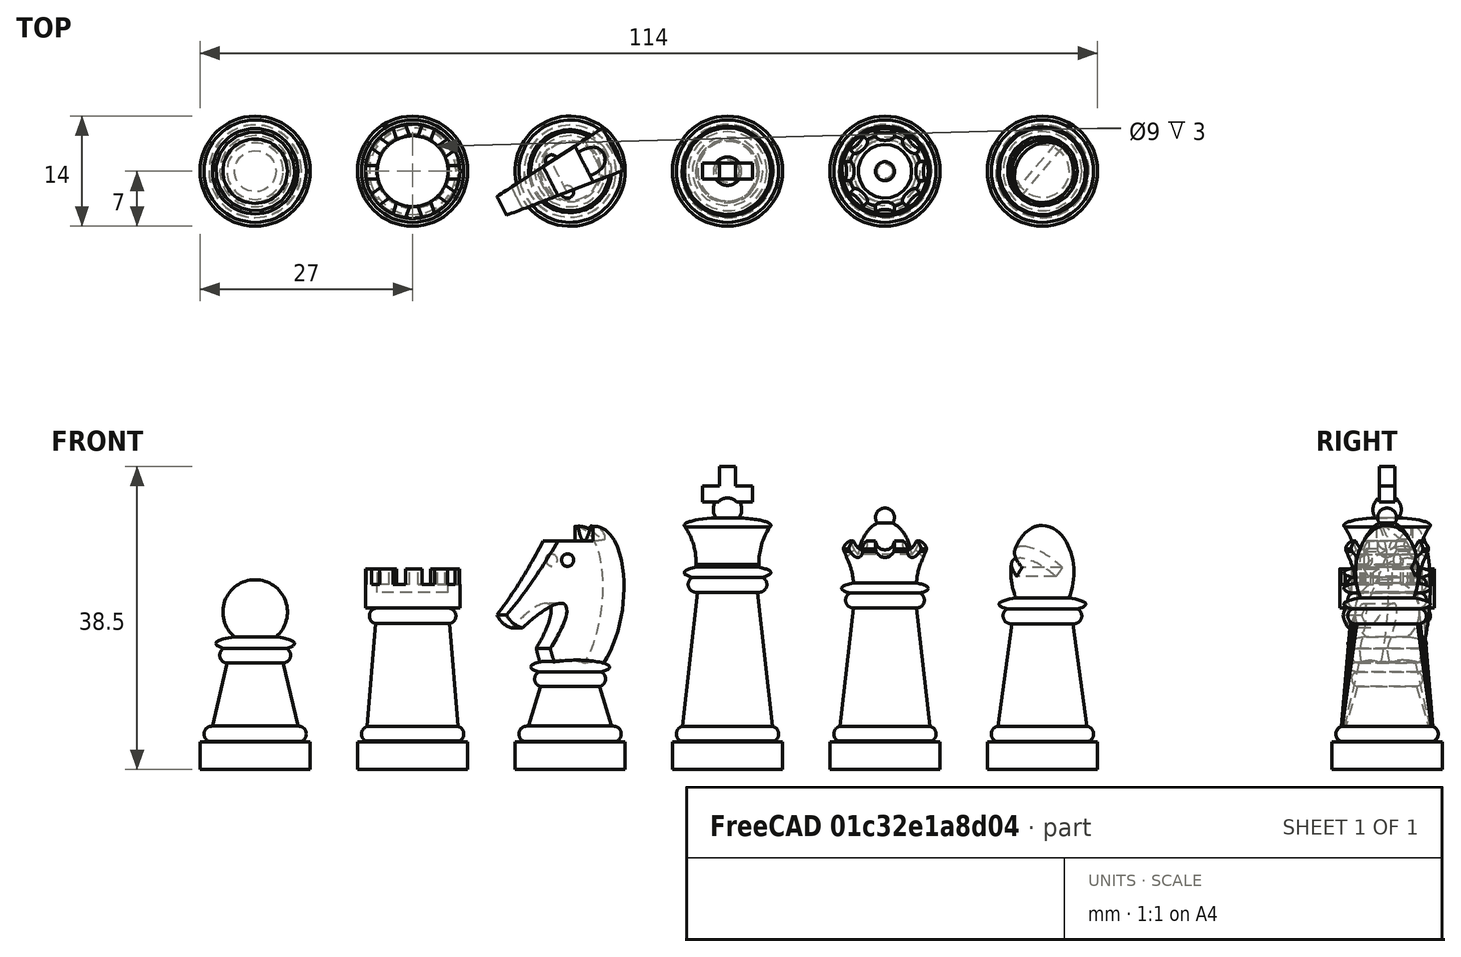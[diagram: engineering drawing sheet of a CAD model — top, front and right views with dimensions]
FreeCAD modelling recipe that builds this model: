
FCSTD DOCUMENT  (FreeCAD 0.15R4671 (Git))
Label: Chess_01
License: All rights reserved
LicenseURL: http://de.wikipedia.org/wiki/Alle_Rechte_vorbehalten
objects: Part::Cut×24, Part::MultiFuse×20, Part::Cylinder×16, Part::Torus×14, Part::Ellipsoid×14, Part::Box×12, Part::Cone×8, Part::Sphere×6, Part::Plane×1, Part::MultiCommon×1
note: 116 computed .brp shape members not serialized (recipe doc carries the construction recipe); baked Part::Feature solids carry a one-line shape summary decoded from their .brp

FEATURE [Part::Cylinder] Cylinder  label="Zylinder"
  Angle = 360
  Height = 3.5
  Radius = 7
FEATURE [Part::Cone] Cone  label="Kegel"
  Angle = 360
  Height = 18
  Placement = pos=(0,0,3) rot=(0,0,1;0rad)
  Radius1 = 6
  Radius2 = 4.5
FEATURE [Part::Cylinder] Cylinder001  label="Zylinder001"
  Angle = 360
  Height = 5
  Placement = pos=(0,0,20.5) rot=(0,0,1;0rad)
  Radius = 6
FEATURE [Part::Torus] Torus
  Angle1 = -180
  Angle2 = 180
  Angle3 = 360
  Placement = pos=(0,0,4.5) rot=(0,0,1;0rad)
  Radius1 = 5.5
  Radius2 = 1
FEATURE [Part::Torus] Torus001
  Angle1 = -180
  Angle2 = 180
  Angle3 = 360
  Placement = pos=(0,0,19.5) rot=(0,0,1;0rad)
  Radius1 = 4.5
  Radius2 = 1
FEATURE [Part::Cylinder] Cylinder002  label="Zylinder002"
  Angle = 360
  Height = 10
  Placement = pos=(0,0,22.5) rot=(0,0,1;0rad)
  Radius = 4.5
FEATURE [Part::Cut] Cut
  Base = -> Cylinder001
  Tool = -> Cylinder002
FEATURE [Part::Box] Box  label="Quader"
  Height = 4
  Length = 14
  Placement = pos=(-7,-1,23.5) rot=(0,0,1;0rad)
  Width = 1.7
FEATURE [Part::Box] Box001  label="Quader001"
  Height = 4
  Length = 14
  Placement = pos=(-5.07533,-4.92351,23.5) rot=(0,0,1;0.628319rad)
  Width = 1.7
FEATURE [Part::Box] Box002  label="Quader002"
  Height = 4
  Length = 14
  Placement = pos=(-1.21206,-6.96641,23.5) rot=(0,0,1;1.25664rad)
  Width = 1.7
FEATURE [Part::Box] Box003  label="Quader003"
  Height = 4
  Length = 14
  Placement = pos=(3.11418,-6.34838,23.5) rot=(0,0,1;1.88496rad)
  Width = 1.7
FEATURE [Part::Box] Box004  label="Quader004"
  Height = 4
  Length = 14
  Placement = pos=(6.2509,-3.30548,23.5) rot=(0,0,1;2.51327rad)
  Width = 1.7
FEATURE [Part::Cut] Cut001
  Base = -> Cut
  Tool = -> Box
FEATURE [Part::Cut] Cut002
  Base = -> Cut001
  Tool = -> Box001
FEATURE [Part::Cut] Cut003
  Base = -> Cut002
  Tool = -> Box002
FEATURE [Part::Cut] Cut004
  Base = -> Cut003
  Tool = -> Box003
FEATURE [Part::Cut] Cut005
  Base = -> Cut004
  Tool = -> Box004
FEATURE [Part::MultiFuse] Fusion
  Shapes = -> [Cone,Cut005]
FEATURE [Part::MultiFuse] Fusion001
  Shapes = -> [Cylinder,Fusion]
FEATURE [Part::MultiFuse] Fusion002
  Shapes = -> [Torus001,Fusion001]
FEATURE [Part::MultiFuse] Fusion003  label="Turm"
  Placement = pos=(40,0,0) rot=(0,0,1;0rad)
  Shapes = -> [Torus,Fusion002]
FEATURE [Part::Cylinder] Cylinder003  label="Zylinder003"
  Angle = 360
  Height = 3.5
  Radius = 7
FEATURE [Part::Cone] Cone001  label="Kegel001"
  Angle = 360
  Height = 18
  Placement = pos=(0,0,3) rot=(0,0,1;0rad)
  Radius1 = 6
  Radius2 = 3.5
FEATURE [Part::Torus] Torus002
  Angle1 = -180
  Angle2 = 180
  Angle3 = 360
  Placement = pos=(0,0,4.5) rot=(0,0,1;0rad)
  Radius1 = 5.5
  Radius2 = 1
FEATURE [Part::Torus] Torus003
  Angle1 = -180
  Angle2 = 180
  Angle3 = 360
  Placement = pos=(0,0,19.5) rot=(0,0,1;0rad)
  Radius1 = 4
  Radius2 = 1
FEATURE [Part::Ellipsoid] Ellipsoid001
  Angle1 = -90
  Angle2 = 90
  Angle3 = 360
  Placement = pos=(0,0,25) rot=(0,0,1;0rad)
  Radius1 = 6
  Radius2 = 4
  Radius3 = 4
FEATURE [Part::Ellipsoid] Ellipsoid
  Angle1 = -90
  Angle2 = 90
  Angle3 = 360
  Placement = pos=(0,0,21) rot=(0,0,1;0rad)
  Radius1 = 1
  Radius2 = 5.5
  Radius3 = 5.5
FEATURE [Part::MultiFuse] Fusion004
  Shapes = -> [Cylinder003,Cone001]
FEATURE [Part::MultiFuse] Fusion005
  Shapes = -> [Fusion004,Torus003]
FEATURE [Part::MultiFuse] Fusion006
  Shapes = -> [Fusion005,Torus002]
FEATURE [Part::MultiFuse] Fusion007
  Shapes = -> [Fusion006,Ellipsoid]
FEATURE [Part::MultiFuse] Fusion008
  Shapes = -> [Fusion007,Ellipsoid001]
FEATURE [Part::Box] Box009  label="Quader005"
  Height = 1.5
  Length = 10
  Placement = pos=(1,-5,24.5) rot=(0,-1,0;0.698132rad)
  Width = 10
FEATURE [Part::Cut] Cut006  label="Laeufer"
  Base = -> Fusion008
  Placement = pos=(120,0,0) rot=(0,0,1;2.44346rad)
  Tool = -> Box009
FEATURE [Part::Plane] Plane  label="Brett"
  Length = 160
  Placement = pos=(-10,-10,0) rot=(0,0,1;0rad)
  Width = 160
FEATURE [Part::Torus] Torus004
  Angle1 = -180
  Angle2 = 180
  Angle3 = 360
  Placement = pos=(0,0,4.5) rot=(0,0,1;0rad)
  Radius1 = 5.5
  Radius2 = 1
FEATURE [Part::Cylinder] Cylinder004  label="Zylinder004"
  Angle = 360
  Height = 3.5
  Radius = 7
FEATURE [Part::Ellipsoid] Ellipsoid002
  Angle1 = -90
  Angle2 = 90
  Angle3 = 360
  Placement = pos=(0,0,25) rot=(0,0,1;0rad)
  Radius1 = 1
  Radius2 = 5.5
  Radius3 = 5.5
FEATURE [Part::Torus] Torus005
  Angle1 = -180
  Angle2 = 180
  Angle3 = 360
  Placement = pos=(0,0,23.5) rot=(0,0,1;0rad)
  Radius1 = 4
  Radius2 = 1
FEATURE [Part::Cone] Cone002  label="Kegel002"
  Angle = 360
  Height = 22
  Placement = pos=(0,0,3) rot=(0,0,1;0rad)
  Radius1 = 6
  Radius2 = 3.5
FEATURE [Part::Ellipsoid] Ellipsoid003
  Angle1 = -90
  Angle2 = 90
  Angle3 = 360
  Placement = pos=(0,0,31) rot=(0,0,1;0rad)
  Radius1 = 1
  Radius2 = 5.5
  Radius3 = 5.5
FEATURE [Part::Cone] Cone003  label="Kegel003"
  Angle = 360
  Height = 9
  Placement = pos=(0,0,22) rot=(0,0,1;0rad)
  Radius1 = 2.8
  Radius2 = 5.5
FEATURE [Part::Torus] Torus006
  Angle1 = -180
  Angle2 = 180
  Angle3 = 360
  Placement = pos=(0,0,26.3) rot=(0,0,1;0rad)
  Radius1 = 12
  Radius2 = 8
FEATURE [Part::Cut] Cut007
  Base = -> Cone003
  Tool = -> Torus006
FEATURE [Part::Sphere] Sphere  label="Kugel"
  Angle1 = -90
  Angle2 = 90
  Angle3 = 360
  Placement = pos=(0,0,33) rot=(0,0,1;0rad)
  Radius = 1.8
FEATURE [Part::Box] Box010  label="Würfel"
  Height = 5.5
  Length = 2
  Placement = pos=(-1,-1,33) rot=(0,0,1;0rad)
  Width = 2
FEATURE [Part::Box] Box011  label="Würfel001"
  Height = 2
  Length = 6.4
  Placement = pos=(-3.2,-1,34) rot=(0,0,1;0rad)
  Width = 2
FEATURE [Part::MultiFuse] Fusion009  label="King"
  Placement = pos=(80,0,0) rot=(0,0,1;0rad)
  Shapes = -> [Torus004,Cone002,Torus005,Box011,Box010,Ellipsoid003,Cylinder004,Ellipsoid002,Sphere,Cut007]
FEATURE [Part::Torus] Torus007
  Angle1 = -180
  Angle2 = 180
  Angle3 = 360
  Placement = pos=(0,0,4.5) rot=(0,0,1;0rad)
  Radius1 = 5.5
  Radius2 = 1
FEATURE [Part::Cylinder] Cylinder005  label="Zylinder005"
  Angle = 360
  Height = 3.5
  Radius = 7
FEATURE [Part::Cone] Cone004  label="Kegel004"
  Angle = 360
  Height = 13
  Placement = pos=(0,0,3) rot=(0,0,1;0rad)
  Radius1 = 6
  Radius2 = 3
FEATURE [Part::Ellipsoid] Ellipsoid004
  Angle1 = -90
  Angle2 = 90
  Angle3 = 360
  Placement = pos=(0,0,16) rot=(0,0,1;0rad)
  Radius1 = 1
  Radius2 = 5
  Radius3 = 5
FEATURE [Part::Torus] Torus008
  Angle1 = -180
  Angle2 = 180
  Angle3 = 360
  Placement = pos=(0,0,14.5) rot=(0,0,1;0rad)
  Radius1 = 3.5
  Radius2 = 1
FEATURE [Part::Sphere] Sphere001  label="Kugel001"
  Angle1 = -90
  Angle2 = 90
  Angle3 = 360
  Placement = pos=(0,0,20) rot=(0,0,1;0rad)
  Radius = 4.1
FEATURE [Part::MultiFuse] Fusion010  label="Bauer"
  Placement = pos=(20,0,0) rot=(0,0,1;0rad)
  Shapes = -> [Torus007,Sphere001,Cylinder005,Torus008,Ellipsoid004,Cone004]
FEATURE [Part::Torus] Torus009
  Angle1 = -180
  Angle2 = 180
  Angle3 = 360
  Placement = pos=(0,0,4.5) rot=(0,0,1;0rad)
  Radius1 = 5.5
  Radius2 = 1
FEATURE [Part::Cone] Cone005  label="Kegel005"
  Angle = 360
  Height = 22
  Placement = pos=(0,0,3) rot=(0,0,1;0rad)
  Radius1 = 6
  Radius2 = 3.5
FEATURE [Part::Torus] Torus010
  Angle1 = -180
  Angle2 = 180
  Angle3 = 360
  Placement = pos=(0,0,21.5) rot=(0,0,1;0rad)
  Radius1 = 4
  Radius2 = 1
FEATURE [Part::Cylinder] Cylinder006  label="Zylinder006"
  Angle = 360
  Height = 3.5
  Radius = 7
FEATURE [Part::Ellipsoid] Ellipsoid005
  Angle1 = -90
  Angle2 = 90
  Angle3 = 360
  Placement = pos=(0,0,23) rot=(0,0,1;0rad)
  Radius1 = 1
  Radius2 = 5.5
  Radius3 = 5.5
FEATURE [Part::Sphere] Sphere002  label="Kugel002"
  Angle1 = -90
  Angle2 = 90
  Angle3 = 360
  Placement = pos=(0,0,32) rot=(0,0,1;0rad)
  Radius = 1.2
FEATURE [Part::Ellipsoid] Ellipsoid006
  Angle1 = -90
  Angle2 = 90
  Angle3 = 360
  Placement = pos=(0,0,28) rot=(0,0,1;0rad)
  Radius1 = 2
  Radius2 = 5.4
  Radius3 = 5.4
FEATURE [Part::Cone] Cone006  label="Kegel006"
  Angle = 360
  Height = 9
  Placement = pos=(0,0,19) rot=(0,0,1;0rad)
  Radius1 = 2.8
  Radius2 = 5.4
FEATURE [Part::Torus] Torus011
  Angle1 = -180
  Angle2 = 180
  Angle3 = 360
  Placement = pos=(0,0,23.3) rot=(0,0,1;0rad)
  Radius1 = 12
  Radius2 = 8
FEATURE [Part::Cut] Cut008
  Base = -> Cone006
  Tool = -> Torus011
FEATURE [Part::Sphere] Sphere003  label="Kugel003"
  Angle1 = -90
  Angle2 = 90
  Angle3 = 360
  Placement = pos=(0,0,31) rot=(0,0,1;0rad)
  Radius = 5
FEATURE [Part::MultiFuse] Fusion011
  Shapes = -> [Cut008,Ellipsoid006]
FEATURE [Part::Cut] Cut009
  Base = -> Fusion011
  Tool = -> Sphere003
FEATURE [Part::Ellipsoid] Ellipsoid007
  Angle1 = -90
  Angle2 = 90
  Angle3 = 360
  Placement = pos=(0,0,26) rot=(0,0,1;0rad)
  Radius1 = 5.5
  Radius2 = 3.5
  Radius3 = 3.5
FEATURE [Part::MultiFuse] Fusion012
  Shapes = -> [Torus009,Cone005,Sphere002,Torus010,Ellipsoid005,Cylinder006,Ellipsoid007]
FEATURE [Part::Cylinder] Cylinder007  label="Zylinder007"
  Angle = 360
  Height = 6
  Placement = pos=(7,0,26.5) rot=(0,-1,0;0.785398rad)
  Radius = 1.2
FEATURE [Part::Cylinder] Cylinder008  label="Zylinder008"
  Angle = 360
  Height = 6
  Placement = pos=(4.94975,4.94975,26.5) rot=(0.281085,-0.678598,0.678598;1.09606rad)
  Radius = 1.2
FEATURE [Part::Cylinder] Cylinder009  label="Zylinder009"
  Angle = 360
  Height = 6
  Placement = pos=(0,7,26.5) rot=(0.357407,-0.357407,0.862856;1.71777rad)
  Radius = 1.2
FEATURE [Part::Cylinder] Cylinder010  label="Zylinder010"
  Angle = 360
  Height = 6
  Placement = pos=(-4.94975,4.94975,26.5) rot=(0.377964,-0.156558,0.912487;2.41886rad)
  Radius = 1.2
FEATURE [Part::Cylinder] Cylinder011  label="Zylinder011"
  Angle = 360
  Height = 6
  Placement = pos=(-7,0,26.5) rot=(0.382683,0,0.92388;3.14159rad)
  Radius = 1.2
FEATURE [Part::Cylinder] Cylinder012  label="Zylinder012"
  Angle = 360
  Height = 6
  Placement = pos=(-4.94975,-4.94975,26.5) rot=(0.377964,0.156558,0.912487;3.86433rad)
  Radius = 1.2
FEATURE [Part::Cylinder] Cylinder013  label="Zylinder013"
  Angle = 360
  Height = 6
  Placement = pos=(0,-7,26.5) rot=(-0.357407,-0.357407,-0.862856;1.71777rad)
  Radius = 1.2
FEATURE [Part::Cylinder] Cylinder014  label="Zylinder014"
  Angle = 360
  Height = 6
  Placement = pos=(4.94975,-4.94975,26.5) rot=(-0.281085,-0.678598,-0.678598;1.09606rad)
  Radius = 1.2
FEATURE [Part::Cut] Cut010
  Base = -> Cut009
  Tool = -> Cylinder007
FEATURE [Part::Cut] Cut011
  Base = -> Cut010
  Tool = -> Cylinder008
FEATURE [Part::Cut] Cut012
  Base = -> Cut011
  Tool = -> Cylinder009
FEATURE [Part::Cut] Cut013
  Base = -> Cut012
  Tool = -> Cylinder010
FEATURE [Part::Cut] Cut014
  Base = -> Cut013
  Tool = -> Cylinder011
FEATURE [Part::Cut] Cut015
  Base = -> Cut014
  Tool = -> Cylinder012
FEATURE [Part::Cut] Cut016
  Base = -> Cut015
  Tool = -> Cylinder013
FEATURE [Part::Cut] Cut017
  Base = -> Cut016
  Tool = -> Cylinder014
FEATURE [Part::MultiFuse] Fusion013  label="Dame"
  Placement = pos=(100,0,0) rot=(0,0,1;0rad)
  Shapes = -> [Fusion012,Cut017]
FEATURE [Part::Cylinder] Cylinder015  label="Zylinder015"
  Angle = 360
  Height = 3.5
  Radius = 7
FEATURE [Part::Cone] Cone007  label="Kegel007"
  Angle = 360
  Height = 10
  Placement = pos=(0,0,3) rot=(0,0,1;0rad)
  Radius1 = 6
  Radius2 = 3
FEATURE [Part::Torus] Torus012
  Angle1 = -180
  Angle2 = 180
  Angle3 = 360
  Placement = pos=(0,0,4.5) rot=(0,0,1;0rad)
  Radius1 = 5.5
  Radius2 = 1
FEATURE [Part::Torus] Torus013
  Angle1 = -180
  Angle2 = 180
  Angle3 = 360
  Placement = pos=(0,0,11.5) rot=(0,0,1;0rad)
  Radius1 = 3.5
  Radius2 = 1
FEATURE [Part::Ellipsoid] Ellipsoid008
  Angle1 = -90
  Angle2 = 90
  Angle3 = 360
  Placement = pos=(0,0,13) rot=(0,0,1;0rad)
  Radius1 = 1
  Radius2 = 5
  Radius3 = 5
FEATURE [Part::Ellipsoid] Ellipsoid009
  Angle1 = -90
  Angle2 = 90
  Angle3 = 360
  Placement = pos=(1,0,21) rot=(0,1,0;0.15708rad)
  Radius1 = 10
  Radius2 = 5
  Radius3 = 40
FEATURE [Part::Box] Box012  label="Würfel002"
  Height = 22
  Length = 22
  Placement = pos=(-13,-5,11) rot=(0,0,1;0rad)
  Width = 10
FEATURE [Part::Ellipsoid] Ellipsoid010  label="Ellipsoid014"
  Angle1 = -90
  Angle2 = 90
  Angle3 = 360
  Placement = pos=(-3.5,0,24.5) rot=(0,1,0;0.785398rad)
  Radius1 = 8
  Radius2 = 5
  Radius3 = 40
FEATURE [Part::Ellipsoid] Ellipsoid011
  Angle1 = -90
  Angle2 = 90
  Angle3 = 360
  Placement = pos=(-6.5,0,32.5) rot=(0,1,0;0.541052rad)
  Radius1 = 20
  Radius2 = 5
  Radius3 = 40
FEATURE [Part::Box] Box013  label="Würfel003"
  Height = 10
  Length = 10
  Placement = pos=(-8,-3,29) rot=(0,0,1;0rad)
  Width = 6
FEATURE [Part::Ellipsoid] Ellipsoid012
  Angle1 = -90
  Angle2 = 90
  Angle3 = 360
  Placement = pos=(-8.5,0,13.5) rot=(0,1,0;0.733038rad)
  Radius1 = 10
  Radius2 = 2.5
  Radius3 = 40
FEATURE [Part::MultiFuse] Fusion015
  Shapes = -> [Cylinder015,Torus013,Ellipsoid008,Cone007,Torus012]
FEATURE [Part::MultiFuse] Fusion016
  Shapes = -> [Ellipsoid010,Ellipsoid009]
FEATURE [Part::Cut] Cut018
  Base = -> Fusion016
  Tool = -> Ellipsoid011
FEATURE [Part::Cut] Cut019
  Base = -> Cut018
  Tool = -> Ellipsoid012
FEATURE [Part::Box] Box014  label="Würfel004"
  Height = 22
  Length = 22
  Placement = pos=(-13,1,11) rot=(0,0,1;0.10472rad)
  Width = 4
FEATURE [Part::MultiCommon] Common
  Shapes = -> [Cut019,Box012]
FEATURE [Part::Box] Box015  label="Würfel005"
  Height = 22
  Length = 22
  Placement = pos=(-13,-5,11) rot=(0,0,-1;0.10472rad)
  Width = 4
FEATURE [Part::Cut] Cut020
  Base = -> Common
  Tool = -> Box015
FEATURE [Part::Cut] Cut021
  Base = -> Cut020
  Tool = -> Box014
FEATURE [Part::Cut] Cut022
  Base = -> Cut021
  Tool = -> Box013
FEATURE [Part::Ellipsoid] Ellipsoid013  label="Ellipsoid015"
  Angle1 = -90
  Angle2 = 90
  Angle3 = 360
  Placement = pos=(3,0,33) rot=(0,0,1;0rad)
  Radius1 = 4
  Radius2 = 6
  Radius3 = 2
FEATURE [Part::Cut] Cut023
  Base = -> Cut022
  Tool = -> Ellipsoid013
FEATURE [Part::Sphere] Sphere004  label="Kugel004"
  Angle1 = -90
  Angle2 = 90
  Angle3 = 360
  Placement = pos=(-1.5,-2.2,26.6) rot=(0,0,1;0rad)
  Radius = 0.8
FEATURE [Part::Sphere] Sphere005  label="Kugel005"
  Angle1 = -90
  Angle2 = 90
  Angle3 = 360
  Placement = pos=(-1.5,2.2,26.6) rot=(0,0,1;0rad)
  Radius = 0.8
FEATURE [Part::MultiFuse] Fusion017
  Shapes = -> [Cut023,Sphere004,Sphere005]
FEATURE [Part::MultiFuse] Fusion018  label="Springer"
  Placement = pos=(60,0,0) rot=(0,0,1;0.471239rad)
  Shapes = -> [Fusion015,Fusion017]
FEATURE [Part::MultiFuse] Fusion019  label="Schwarz"
  Shapes = -> [Fusion010,Fusion018,Fusion013]
FEATURE [Part::MultiFuse] Fusion020  label="Weiss"
  Shapes = -> [Fusion009,Fusion003,Cut006]
